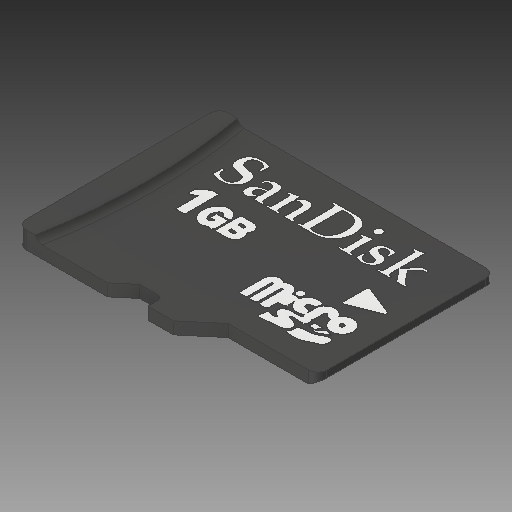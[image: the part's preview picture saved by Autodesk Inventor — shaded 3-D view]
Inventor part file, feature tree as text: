
AUTODESK INVENTOR PART (.ipt)
format: ipt  version: 2018.2 (Build 222227000, 227)  size: 699,904 bytes
history: native  units: mm
features: chamfer x1
ambient origin geometry x8: Origin, YZ Plane, XZ Plane, XY Plane, X Axis, Y Axis, Z Axis, Center Point
bodies: Solido1 (feature_tree)
feature tree (1):
  chamfer  "Chamfer1"  [1 undecoded]
note: 1 required parameter value undecoded (feature->parameter linkage not recoverable at this tier; creation-order binding heuristic only, values carry confidence <= 0.55)
